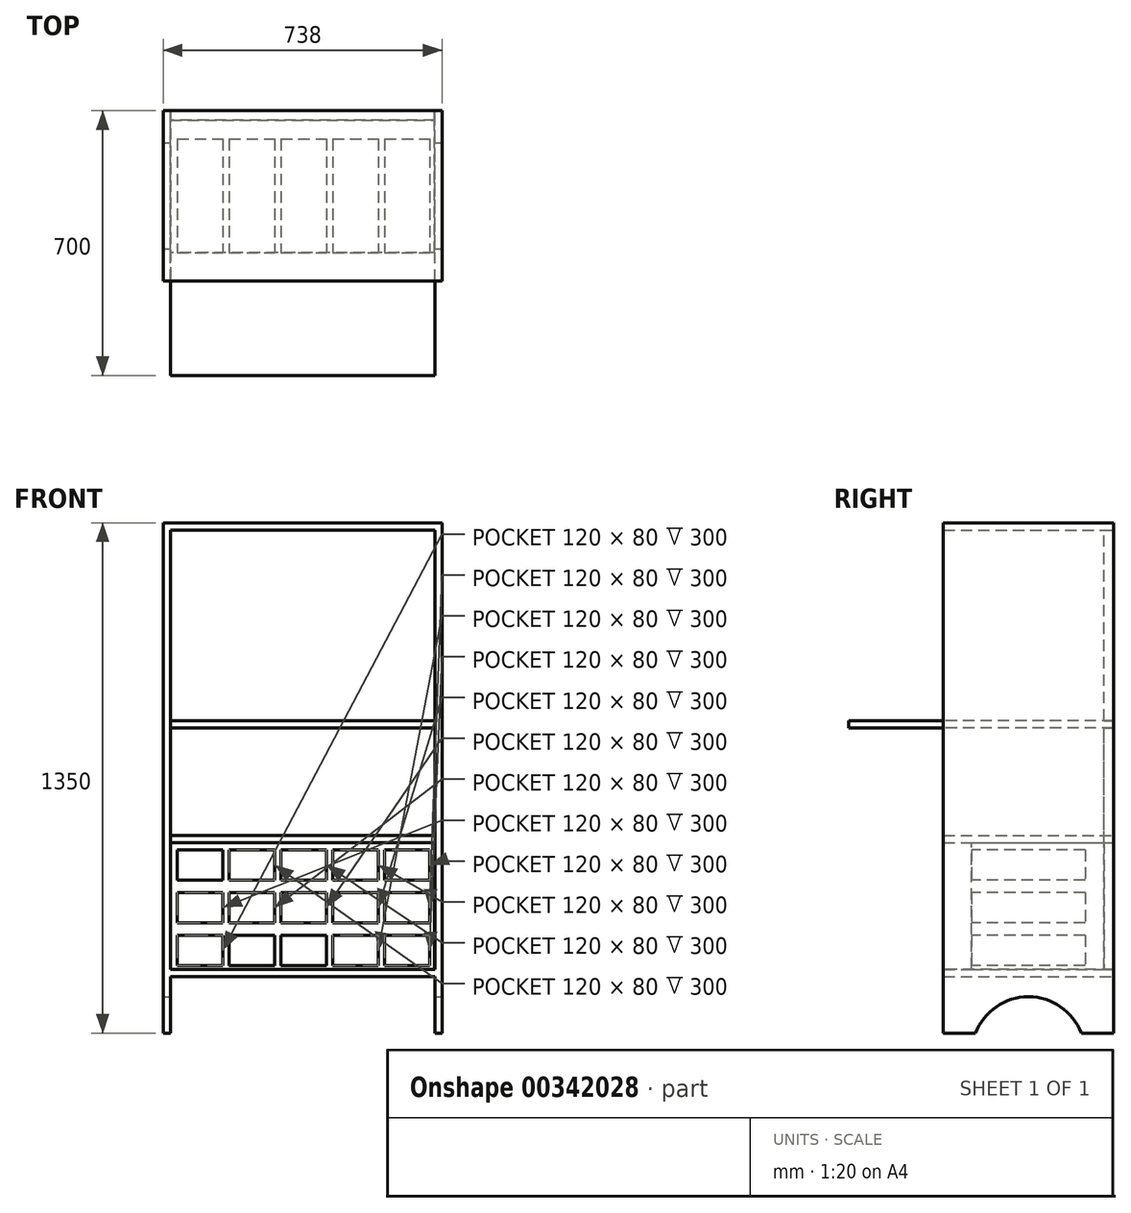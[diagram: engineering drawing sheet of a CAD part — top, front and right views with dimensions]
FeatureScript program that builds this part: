
annotation { "Feature Type Name" : "Feature", "Feature Type Description" : "" }
export const myFeature = defineFeature(function(context is Context, id is Id, definition is map)
    precondition{}
    {
        {
            var Q0;
            Q0=qCreatedBy(makeId("Front.planeOp"),FACE);
            var sketch = newSketch(context, id + "F0", { "sketchPlane" : qUnion([Q0])});
            skLineSegment(sketch, "E0.bottom", {"start": v(-369, 0) * mm, "end": v(-350, 0) * mm});
            skLineSegment(sketch, "E0.top", {"start": v(-369, 1350) * mm, "end": v(-350, 1350) * mm});
            skLineSegment(sketch, "E0.left", {"start": v(-369, 0) * mm, "end": v(-369, 1350) * mm});
            skLineSegment(sketch, "E0.right", {"start": v(-350, 0) * mm, "end": v(-350, 1350) * mm});
            skLineSegment(sketch, "E1", {"start": v(0, 1331) * mm, "end": v(0, 0) * mm, "construction": true});
            skLineSegment(sketch, "E2.MirrorCS", {"start": v(350, 0) * mm, "end": v(350, 1350) * mm});
            skLineSegment(sketch, "E3.MirrorCS", {"start": v(369, 0) * mm, "end": v(350, 0) * mm});
            skLineSegment(sketch, "E4.MirrorCS", {"start": v(369, 0) * mm, "end": v(369, 1350) * mm});
            skLineSegment(sketch, "E5.MirrorCS", {"start": v(369, 1350) * mm, "end": v(350, 1350) * mm});
            skLineSegment(sketch, "E6.bottom", {"start": v(-350, 1350) * mm, "end": v(350, 1350) * mm});
            skLineSegment(sketch, "E6.top", {"start": v(-350, 1331) * mm, "end": v(350, 1331) * mm});
            skLineSegment(sketch, "E6.left", {"start": v(-350, 1350) * mm, "end": v(-350, 1331) * mm});
            skLineSegment(sketch, "E6.right", {"start": v(350, 1350) * mm, "end": v(350, 1331) * mm});
            skSolve(sketch);
        }
        {
            var Q0;
            Q0 = qSketchRegion(id + "F0", true);
            extrude(context, id + "F1", {"entities" : qUnion([Q0]), "depth" : 450 * mm});
        }
        {
            var Q0;
            Q0=makeQuery(id+"F1.opExtrude","SWEPT_FACE",FACE,{"disambiguationData":[OSD([sQuery(id+"F0.wireOp",EDGE,"E0.right")])]});
            var sketch = newSketch(context, id + "F2", { "sketchPlane" : qUnion([Q0])});
            skLineSegment(sketch, "E7.bottom", {"start": v(-450, 826.75) * mm, "end": v(0, 826.75) * mm});
            skLineSegment(sketch, "E7.top", {"start": v(-450, 807.75) * mm, "end": v(0, 807.75) * mm});
            skLineSegment(sketch, "E7.left", {"start": v(-450, 826.75) * mm, "end": v(-450, 807.75) * mm});
            skLineSegment(sketch, "E7.right", {"start": v(0, 826.75) * mm, "end": v(0, 807.75) * mm});
            skLineSegment(sketch, "E8.bottom", {"start": v(-450, 169) * mm, "end": v(0, 169) * mm});
            skLineSegment(sketch, "E8.top", {"start": v(-450, 150) * mm, "end": v(0, 150) * mm});
            skLineSegment(sketch, "E8.left", {"start": v(-450, 169) * mm, "end": v(-450, 150) * mm});
            skLineSegment(sketch, "E8.right", {"start": v(0, 169) * mm, "end": v(0, 150) * mm});
            skSolve(sketch);
        }
        {
            var Q0;
            Q0=makeQuery(id+"F2.imprint","IMPRINT",FACE,{"disambiguationData":[TD([[makeQuery(id+"F2.imprint","IMPRINT",EDGE,{"derivedFrom":sQuery(id+"F2.wireOp",EDGE,"E7.bottom")}),-1.0]])]});
            var Q1;
            Q1=makeQuery(id+"F2.imprint","IMPRINT",FACE,{"disambiguationData":[TD([[makeQuery(id+"F2.imprint","IMPRINT",EDGE,{"derivedFrom":sQuery(id+"F2.wireOp",EDGE,"E8.bottom")}),-1.0]])]});
            var Q2;
            Q2=qCreatedBy(makeId("Right.planeOp"),FACE);
            extrude(context, id + "F3", {"entities" : qUnion([Q0, Q1]), "operationType" : NewBodyOperationType.ADD, "endBound" : BoundingType.UP_TO_NEXT, "endBoundEntityFace" : qUnion([Q2]), "depth" : 25 * mm});
        }
        {
            var Q0;
            Q0=makeQuery(id+"F3.boolean.opBoolean","MERGE",FACE,{"derivedFrom":[makeQuery(id+"F1.opExtrude","CAP_FACE",FACE,{"disambiguationData":[OSD([sQuery(id+"F0.wireOp",EDGE,"E0.bottom"),sQuery(id+"F0.wireOp",EDGE,"E0.top"),sQuery(id+"F0.wireOp",EDGE,"E0.left"),sQuery(id+"F0.wireOp",EDGE,"E0.right"),sQuery(id+"F0.wireOp",EDGE,"KUvRnLVw-DjVN-ga7X-LMZa-ZJt3v3Kkx2uW.bottom"),sQuery(id+"F0.wireOp",EDGE,"KUvRnLVw-DjVN-ga7X-LMZa-ZJt3v3Kkx2uW.top"),sQuery(id+"F0.wireOp",EDGE,"KUvRnLVw-DjVN-ga7X-LMZa-ZJt3v3Kkx2uW.right")])],"isStart":true}),makeQuery(id+"F3.opExtrude","SWEPT_FACE",FACE,{"disambiguationData":[OSD([sQuery(id+"F2.wireOp",EDGE,"E7.right")])]})]});
            var sketch = newSketch(context, id + "F4", { "sketchPlane" : qUnion([Q0])});
            skLineSegment(sketch, "E9.bottom", {"start": v(350, 504.2) * mm, "end": v(-348.68, 504.2) * mm});
            skLineSegment(sketch, "E9.top", {"start": v(350, 154.2) * mm, "end": v(-348.68, 154.2) * mm});
            skLineSegment(sketch, "E9.left", {"start": v(350, 504.2) * mm, "end": v(350, 154.2) * mm});
            skLineSegment(sketch, "E9.right", {"start": v(-348.68, 504.2) * mm, "end": v(-348.68, 154.2) * mm});
            skSolve(sketch);
        }
        {
            var Q0;
            Q0=makeQuery(id+"F4.imprint","IMPRINT",FACE,{"disambiguationData":[TD([[makeQuery(id+"F4.imprint","IMPRINT",EDGE,{"derivedFrom":sQuery(id+"F4.wireOp",EDGE,"E9.bottom")}),1.0]])]});
            extrude(context, id + "F5", {"entities" : qUnion([Q0]), "operationType" : NewBodyOperationType.ADD, "oppositeDirection" : true, "depth" : 375 * mm});
        }
        {
            var Q0;
            Q0=makeQuery(id+"F5.opExtrude","CAP_FACE",FACE,{"disambiguationData":[OSD([sQuery(id+"F4.wireOp",EDGE,"E9.bottom"),sQuery(id+"F4.wireOp",EDGE,"E9.top"),sQuery(id+"F4.wireOp",EDGE,"E9.left"),sQuery(id+"F4.wireOp",EDGE,"E9.right")])],"isStart":false});
            var sketch = newSketch(context, id + "F6", { "sketchPlane" : qUnion([Q0])});
            skLineSegment(sketch, "E10.bottom", {"start": v(-331, 485.2) * mm, "end": v(-211, 485.2) * mm});
            skLineSegment(sketch, "E10.top", {"start": v(-331, 405.2) * mm, "end": v(-211, 405.2) * mm});
            skLineSegment(sketch, "E10.left", {"start": v(-331, 485.2) * mm, "end": v(-331, 405.2) * mm});
            skLineSegment(sketch, "E10.right", {"start": v(-211, 485.2) * mm, "end": v(-211, 405.2) * mm});
            skLineSegment(sketch, "E11.0.1.0", {"start": v(-331, 372) * mm, "end": v(-211, 372) * mm});
            skLineSegment(sketch, "E11.0.1.1", {"start": v(-211, 372) * mm, "end": v(-211, 292) * mm});
            skLineSegment(sketch, "E11.0.1.2", {"start": v(-331, 292) * mm, "end": v(-211, 292) * mm});
            skLineSegment(sketch, "E11.0.1.3", {"start": v(-331, 372) * mm, "end": v(-331, 292) * mm});
            skLineSegment(sketch, "E11.0.2.0", {"start": v(-331, 258.8) * mm, "end": v(-211, 258.8) * mm});
            skLineSegment(sketch, "E11.0.2.1", {"start": v(-211, 258.8) * mm, "end": v(-211, 178.8) * mm});
            skLineSegment(sketch, "E11.0.2.2", {"start": v(-331, 178.8) * mm, "end": v(-211, 178.8) * mm});
            skLineSegment(sketch, "E11.0.2.3", {"start": v(-331, 258.8) * mm, "end": v(-331, 178.8) * mm});
            skLineSegment(sketch, "E11.1.0.0", {"start": v(-194, 485.02) * mm, "end": v(-74, 485.02) * mm});
            skLineSegment(sketch, "E11.1.0.1", {"start": v(-74, 485.02) * mm, "end": v(-74, 405.02) * mm});
            skLineSegment(sketch, "E11.1.0.2", {"start": v(-194, 405.02) * mm, "end": v(-74, 405.02) * mm});
            skLineSegment(sketch, "E11.1.0.3", {"start": v(-194, 485.02) * mm, "end": v(-194, 405.02) * mm});
            skLineSegment(sketch, "E11.1.1.0", {"start": v(-194, 371.82) * mm, "end": v(-74, 371.82) * mm});
            skLineSegment(sketch, "E11.1.1.1", {"start": v(-74, 371.82) * mm, "end": v(-74, 291.82) * mm});
            skLineSegment(sketch, "E11.1.1.2", {"start": v(-194, 291.82) * mm, "end": v(-74, 291.82) * mm});
            skLineSegment(sketch, "E11.1.1.3", {"start": v(-194, 371.82) * mm, "end": v(-194, 291.82) * mm});
            skLineSegment(sketch, "E11.1.2.0", {"start": v(-194, 258.62) * mm, "end": v(-74, 258.62) * mm});
            skLineSegment(sketch, "E11.1.2.1", {"start": v(-74, 258.62) * mm, "end": v(-74, 178.62) * mm});
            skLineSegment(sketch, "E11.1.2.2", {"start": v(-194, 178.62) * mm, "end": v(-74, 178.62) * mm});
            skLineSegment(sketch, "E11.1.2.3", {"start": v(-194, 258.62) * mm, "end": v(-194, 178.62) * mm});
            skLineSegment(sketch, "E11.2.0.0", {"start": v(-57, 484.83) * mm, "end": v(63, 484.83) * mm});
            skLineSegment(sketch, "E11.2.0.1", {"start": v(63, 484.83) * mm, "end": v(63, 404.83) * mm});
            skLineSegment(sketch, "E11.2.0.2", {"start": v(-57, 404.83) * mm, "end": v(63, 404.83) * mm});
            skLineSegment(sketch, "E11.2.0.3", {"start": v(-57, 484.83) * mm, "end": v(-57, 404.83) * mm});
            skLineSegment(sketch, "E11.2.1.0", {"start": v(-57, 371.64) * mm, "end": v(63, 371.64) * mm});
            skLineSegment(sketch, "E11.2.1.1", {"start": v(63, 371.64) * mm, "end": v(63, 291.64) * mm});
            skLineSegment(sketch, "E11.2.1.2", {"start": v(-57, 291.64) * mm, "end": v(63, 291.64) * mm});
            skLineSegment(sketch, "E11.2.1.3", {"start": v(-57, 371.64) * mm, "end": v(-57, 291.64) * mm});
            skLineSegment(sketch, "E11.2.2.0", {"start": v(-57, 258.44) * mm, "end": v(63, 258.44) * mm});
            skLineSegment(sketch, "E11.2.2.1", {"start": v(63, 258.44) * mm, "end": v(63, 178.44) * mm});
            skLineSegment(sketch, "E11.2.2.2", {"start": v(-57, 178.44) * mm, "end": v(63, 178.44) * mm});
            skLineSegment(sketch, "E11.2.2.3", {"start": v(-57, 258.44) * mm, "end": v(-57, 178.44) * mm});
            skLineSegment(sketch, "E11.3.0.0", {"start": v(80, 484.65) * mm, "end": v(200, 484.65) * mm});
            skLineSegment(sketch, "E11.3.0.1", {"start": v(200, 484.65) * mm, "end": v(200, 404.65) * mm});
            skLineSegment(sketch, "E11.3.0.2", {"start": v(80, 404.65) * mm, "end": v(200, 404.65) * mm});
            skLineSegment(sketch, "E11.3.0.3", {"start": v(80, 484.65) * mm, "end": v(80, 404.65) * mm});
            skLineSegment(sketch, "E11.3.1.0", {"start": v(80, 371.45) * mm, "end": v(200, 371.45) * mm});
            skLineSegment(sketch, "E11.3.1.1", {"start": v(200, 371.45) * mm, "end": v(200, 291.45) * mm});
            skLineSegment(sketch, "E11.3.1.2", {"start": v(80, 291.45) * mm, "end": v(200, 291.45) * mm});
            skLineSegment(sketch, "E11.3.1.3", {"start": v(80, 371.45) * mm, "end": v(80, 291.45) * mm});
            skLineSegment(sketch, "E11.3.2.0", {"start": v(80, 258.26) * mm, "end": v(200, 258.26) * mm});
            skLineSegment(sketch, "E11.3.2.1", {"start": v(200, 258.26) * mm, "end": v(200, 178.26) * mm});
            skLineSegment(sketch, "E11.3.2.2", {"start": v(80, 178.26) * mm, "end": v(200, 178.26) * mm});
            skLineSegment(sketch, "E11.3.2.3", {"start": v(80, 258.26) * mm, "end": v(80, 178.26) * mm});
            skLineSegment(sketch, "E11.4.0.0", {"start": v(217, 484.47) * mm, "end": v(337, 484.47) * mm});
            skLineSegment(sketch, "E11.4.0.1", {"start": v(337, 484.47) * mm, "end": v(337, 404.47) * mm});
            skLineSegment(sketch, "E11.4.0.2", {"start": v(217, 404.47) * mm, "end": v(337, 404.47) * mm});
            skLineSegment(sketch, "E11.4.0.3", {"start": v(217, 484.47) * mm, "end": v(217, 404.47) * mm});
            skLineSegment(sketch, "E11.4.1.0", {"start": v(217, 371.27) * mm, "end": v(337, 371.27) * mm});
            skLineSegment(sketch, "E11.4.1.1", {"start": v(337, 371.27) * mm, "end": v(337, 291.27) * mm});
            skLineSegment(sketch, "E11.4.1.2", {"start": v(217, 291.27) * mm, "end": v(337, 291.27) * mm});
            skLineSegment(sketch, "E11.4.1.3", {"start": v(217, 371.27) * mm, "end": v(217, 291.27) * mm});
            skLineSegment(sketch, "E11.4.2.0", {"start": v(217, 258.07) * mm, "end": v(337, 258.07) * mm});
            skLineSegment(sketch, "E11.4.2.1", {"start": v(337, 258.07) * mm, "end": v(337, 178.07) * mm});
            skLineSegment(sketch, "E11.4.2.2", {"start": v(217, 178.07) * mm, "end": v(337, 178.07) * mm});
            skLineSegment(sketch, "E11.4.2.3", {"start": v(217, 258.07) * mm, "end": v(217, 178.07) * mm});
            skLineSegment(sketch, "E11.direction1", {"start": v(-331, 485.2) * mm, "end": v(-194, 485.02) * mm, "construction": true});
            skLineSegment(sketch, "E11.direction2", {"start": v(-331, 485.2) * mm, "end": v(-331, 372) * mm, "construction": true});
            skSolve(sketch);
        }
        {
            var Q0;
            Q0=makeQuery(id+"F6.imprint","IMPRINT",FACE,{"disambiguationData":[TD([[makeQuery(id+"F6.imprint","IMPRINT",EDGE,{"derivedFrom":sQuery(id+"F6.wireOp",EDGE,"E10.bottom")}),-1.0]])]});
            var Q1;
            Q1=makeQuery(id+"F6.imprint","IMPRINT",FACE,{"disambiguationData":[TD([[makeQuery(id+"F6.imprint","IMPRINT",EDGE,{"derivedFrom":sQuery(id+"F6.wireOp",EDGE,"E11.1.0.0")}),-1.0]])]});
            var Q2;
            Q2=makeQuery(id+"F6.imprint","IMPRINT",FACE,{"disambiguationData":[TD([[makeQuery(id+"F6.imprint","IMPRINT",EDGE,{"derivedFrom":sQuery(id+"F6.wireOp",EDGE,"E11.2.0.0")}),-1.0]])]});
            var Q3;
            Q3=makeQuery(id+"F6.imprint","IMPRINT",FACE,{"disambiguationData":[TD([[makeQuery(id+"F6.imprint","IMPRINT",EDGE,{"derivedFrom":sQuery(id+"F6.wireOp",EDGE,"E11.3.0.0")}),-1.0]])]});
            var Q4;
            Q4=makeQuery(id+"F6.imprint","IMPRINT",FACE,{"disambiguationData":[TD([[makeQuery(id+"F6.imprint","IMPRINT",EDGE,{"derivedFrom":sQuery(id+"F6.wireOp",EDGE,"E11.4.0.0")}),-1.0]])]});
            var Q5;
            Q5=makeQuery(id+"F6.imprint","IMPRINT",FACE,{"disambiguationData":[TD([[makeQuery(id+"F6.imprint","IMPRINT",EDGE,{"derivedFrom":sQuery(id+"F6.wireOp",EDGE,"E11.0.1.0")}),-1.0]])]});
            var Q6;
            Q6=makeQuery(id+"F6.imprint","IMPRINT",FACE,{"disambiguationData":[TD([[makeQuery(id+"F6.imprint","IMPRINT",EDGE,{"derivedFrom":sQuery(id+"F6.wireOp",EDGE,"E11.1.1.0")}),-1.0]])]});
            var Q7;
            Q7=makeQuery(id+"F6.imprint","IMPRINT",FACE,{"disambiguationData":[TD([[makeQuery(id+"F6.imprint","IMPRINT",EDGE,{"derivedFrom":sQuery(id+"F6.wireOp",EDGE,"E11.2.1.0")}),-1.0]])]});
            var Q8;
            Q8=makeQuery(id+"F6.imprint","IMPRINT",FACE,{"disambiguationData":[TD([[makeQuery(id+"F6.imprint","IMPRINT",EDGE,{"derivedFrom":sQuery(id+"F6.wireOp",EDGE,"E11.3.1.0")}),-1.0]])]});
            var Q9;
            Q9=makeQuery(id+"F6.imprint","IMPRINT",FACE,{"disambiguationData":[TD([[makeQuery(id+"F6.imprint","IMPRINT",EDGE,{"derivedFrom":sQuery(id+"F6.wireOp",EDGE,"E11.4.1.0")}),-1.0]])]});
            var Q10;
            Q10=makeQuery(id+"F6.imprint","IMPRINT",FACE,{"disambiguationData":[TD([[makeQuery(id+"F6.imprint","IMPRINT",EDGE,{"derivedFrom":sQuery(id+"F6.wireOp",EDGE,"E11.0.2.0")}),-1.0]])]});
            var Q11;
            Q11=makeQuery(id+"F6.imprint","IMPRINT",FACE,{"disambiguationData":[TD([[makeQuery(id+"F6.imprint","IMPRINT",EDGE,{"derivedFrom":sQuery(id+"F6.wireOp",EDGE,"E11.1.2.0")}),-1.0]])]});
            var Q12;
            Q12=makeQuery(id+"F6.imprint","IMPRINT",FACE,{"disambiguationData":[TD([[makeQuery(id+"F6.imprint","IMPRINT",EDGE,{"derivedFrom":sQuery(id+"F6.wireOp",EDGE,"E11.2.2.0")}),-1.0]])]});
            var Q13;
            Q13=makeQuery(id+"F6.imprint","IMPRINT",FACE,{"disambiguationData":[TD([[makeQuery(id+"F6.imprint","IMPRINT",EDGE,{"derivedFrom":sQuery(id+"F6.wireOp",EDGE,"E11.3.2.0")}),-1.0]])]});
            var Q14;
            Q14=makeQuery(id+"F6.imprint","IMPRINT",FACE,{"disambiguationData":[TD([[makeQuery(id+"F6.imprint","IMPRINT",EDGE,{"derivedFrom":sQuery(id+"F6.wireOp",EDGE,"E11.4.2.0")}),-1.0]])]});
            extrude(context, id + "F7", {"entities" : qUnion([Q0, Q1, Q2, Q3, Q4, Q5, Q6, Q7, Q8, Q9, Q10, Q11, Q12, Q13, Q14]), "operationType" : NewBodyOperationType.REMOVE, "oppositeDirection" : true, "depth" : 300 * mm});
        }
        {
            var Q0;
            Q0=makeQuery(id+"F1.opExtrude","SWEPT_FACE",FACE,{"disambiguationData":[OSD([sQuery(id+"F0.wireOp",EDGE,"E4.MirrorCS")])]});
            var sketch = newSketch(context, id + "F8", { "sketchPlane" : qUnion([Q0])});
            skArc(sketch, "E12", {"start": v(-85, 0) * mm, "mid": v(-225, 96.15) * mm, "end": v(-365, 0) * mm});
            skLineSegment(sketch, "E13", {"start": v(-365, 0) * mm, "end": v(-85, 0) * mm});
            skSolve(sketch);
        }
        {
            var Q0;
            Q0 = qSketchRegion(id + "F8", true);
            extrude(context, id + "F9", {"entities" : qUnion([Q0]), "operationType" : NewBodyOperationType.REMOVE, "endBound" : BoundingType.THROUGH_ALL, "oppositeDirection" : true, "depth" : 25 * mm});
        }
        {
            var Q0;
            {var subQ0=sQuery(id+"F2.wireOp",EDGE,"E8.right");var subQ1=sQuery(id+"F0.wireOp",EDGE,"E0.right");Q0=makeQuery(id+"F5.boolean.opBoolean","MERGE",FACE,{"derivedFrom":[makeQuery(id+"F3.boolean.opBoolean","MERGE",FACE,{"derivedFrom":[makeQuery(id+"F1.opExtrude","CAP_FACE",FACE,{"disambiguationData":[OSD([sQuery(id+"F0.wireOp",EDGE,"E0.bottom"),sQuery(id+"F0.wireOp",EDGE,"E0.top"),sQuery(id+"F0.wireOp",EDGE,"E0.left"),subQ1,sQuery(id+"F0.wireOp",EDGE,"E2.MirrorCS"),sQuery(id+"F0.wireOp",EDGE,"E3.MirrorCS"),sQuery(id+"F0.wireOp",EDGE,"E4.MirrorCS"),sQuery(id+"F0.wireOp",EDGE,"E5.MirrorCS"),sQuery(id+"F0.wireOp",EDGE,"E6.bottom"),sQuery(id+"F0.wireOp",EDGE,"E6.top")])],"isStart":true}),makeQuery(id+"F3.opExtrude","SWEPT_FACE",FACE,{"disambiguationData":[OSD([sQuery(id+"F2.wireOp",EDGE,"E7.right")])]}),makeQuery(id+"F3.opExtrude","SWEPT_FACE",FACE,{"disambiguationData":[OSD([subQ0])]})]}),makeQuery(id+"F5.opExtrude","CAP_FACE",FACE,{"disambiguationData":[OSD([subQ1,sQuery(id+"F2.wireOp",EDGE,"E8.bottom"),subQ0,sQuery(id+"F4.wireOp",EDGE,"E9.bottom"),sQuery(id+"F4.wireOp",EDGE,"E9.left"),sQuery(id+"F4.wireOp",EDGE,"E9.right")])],"isStart":true})]});}
            var sketch = newSketch(context, id + "F10", { "sketchPlane" : qUnion([Q0])});
            skLineSegment(sketch, "E14.bottom", {"start": v(-350, 1331) * mm, "end": v(350, 1331) * mm});
            skLineSegment(sketch, "E14.top", {"start": v(-350, 826.75) * mm, "end": v(350, 826.75) * mm});
            skLineSegment(sketch, "E14.left", {"start": v(-350, 1331) * mm, "end": v(-350, 826.75) * mm});
            skLineSegment(sketch, "E14.right", {"start": v(350, 1331) * mm, "end": v(350, 826.75) * mm});
            skSolve(sketch);
        }
        {
            var Q0;
            Q0=makeQuery(id+"F10.imprint","IMPRINT",FACE,{"disambiguationData":[TD([[makeQuery(id+"F10.imprint","IMPRINT",EDGE,{"derivedFrom":sQuery(id+"F10.wireOp",EDGE,"E14.bottom")}),1.0]])]});
            extrude(context, id + "F11", {"entities" : qUnion([Q0]), "oppositeDirection" : true, "depth" : 25 * mm});
        }
        {
            var Q0;
            {var subQ0=sQuery(id+"F2.wireOp",EDGE,"E8.right");var subQ1=sQuery(id+"F0.wireOp",EDGE,"E0.right");Q0=makeQuery(id+"F5.boolean.opBoolean","MERGE",FACE,{"derivedFrom":[makeQuery(id+"F3.boolean.opBoolean","MERGE",FACE,{"derivedFrom":[makeQuery(id+"F1.opExtrude","CAP_FACE",FACE,{"disambiguationData":[OSD([sQuery(id+"F0.wireOp",EDGE,"E0.bottom"),sQuery(id+"F0.wireOp",EDGE,"E0.top"),sQuery(id+"F0.wireOp",EDGE,"E0.left"),subQ1,sQuery(id+"F0.wireOp",EDGE,"E2.MirrorCS"),sQuery(id+"F0.wireOp",EDGE,"E3.MirrorCS"),sQuery(id+"F0.wireOp",EDGE,"E4.MirrorCS"),sQuery(id+"F0.wireOp",EDGE,"E5.MirrorCS"),sQuery(id+"F0.wireOp",EDGE,"E6.bottom"),sQuery(id+"F0.wireOp",EDGE,"E6.top")])],"isStart":true}),makeQuery(id+"F3.opExtrude","SWEPT_FACE",FACE,{"disambiguationData":[OSD([sQuery(id+"F2.wireOp",EDGE,"E7.right")])]}),makeQuery(id+"F3.opExtrude","SWEPT_FACE",FACE,{"disambiguationData":[OSD([subQ0])]})]}),makeQuery(id+"F5.opExtrude","CAP_FACE",FACE,{"disambiguationData":[OSD([subQ1,sQuery(id+"F2.wireOp",EDGE,"E8.bottom"),subQ0,sQuery(id+"F4.wireOp",EDGE,"E9.bottom"),sQuery(id+"F4.wireOp",EDGE,"E9.left"),sQuery(id+"F4.wireOp",EDGE,"E9.right")])],"isStart":true})]});}
            var sketch = newSketch(context, id + "F12", { "sketchPlane" : qUnion([Q0])});
            skSolve(sketch);
        }
        {
            var Q0;
            Q0=makeQuery(id+"F12.imprint","IMPRINT",FACE,{"disambiguationData":[TD([[makeQuery(id+"F12.imprint","IMPRINT",EDGE,{"derivedFrom":makeQuery(id+"F5.opExtrude","CAP_EDGE",EDGE,{"disambiguationData":[OSD([sQuery(id+"F4.wireOp",EDGE,"E9.bottom")])],"isStart":true})}),-1.0]])]});
            extrude(context, id + "F13", {"entities" : qUnion([Q0]), "oppositeDirection" : true, "depth" : 25 * mm});
        }
        {
            var Q0;
            {var subQ6=sQuery(id+"F0.wireOp",EDGE,"E0.right");Q0=makeQuery(id+"F3.boolean.opBoolean","SPLIT",FACE,{"disambiguationData":[TD([makeQuery(id+"F3.opExtrude","SWEPT_FACE",FACE,{"disambiguationData":[OSD([sQuery(id+"F2.wireOp",EDGE,"E7.top")])]})])],"derivedFrom":makeQuery(id+"F1.opExtrude","SWEPT_FACE",FACE,{"disambiguationData":[OSD([subQ6])]})});}
            var sketch = newSketch(context, id + "F14", { "sketchPlane" : qUnion([Q0])});
            skLineSegment(sketch, "E15.bottom", {"start": v(0, 523.2) * mm, "end": v(-450, 523.2) * mm});
            skLineSegment(sketch, "E15.top", {"start": v(0, 504.2) * mm, "end": v(-450, 504.2) * mm});
            skLineSegment(sketch, "E15.left", {"start": v(0, 523.2) * mm, "end": v(0, 504.2) * mm});
            skLineSegment(sketch, "E15.right", {"start": v(-450, 523.2) * mm, "end": v(-450, 504.2) * mm});
            skSolve(sketch);
        }
        {
            var Q0;
            Q0=makeQuery(id+"F14.imprint","IMPRINT",FACE,{"disambiguationData":[TD([[makeQuery(id+"F14.imprint","IMPRINT",EDGE,{"derivedFrom":sQuery(id+"F14.wireOp",EDGE,"E15.bottom")}),1.0]])]});
            extrude(context, id + "F15", {"entities" : qUnion([Q0]), "endBound" : BoundingType.UP_TO_NEXT, "depth" : 25 * mm});
        }
        {
            var Q0;
            Q0=makeQuery(id+"F3.boolean.opBoolean","MERGE",FACE,{"derivedFrom":[makeQuery(id+"F1.opExtrude","CAP_FACE",FACE,{"disambiguationData":[OSD([sQuery(id+"F0.wireOp",EDGE,"E0.bottom"),sQuery(id+"F0.wireOp",EDGE,"E0.top"),sQuery(id+"F0.wireOp",EDGE,"E0.left"),sQuery(id+"F0.wireOp",EDGE,"E0.right"),sQuery(id+"F0.wireOp",EDGE,"E2.MirrorCS"),sQuery(id+"F0.wireOp",EDGE,"E3.MirrorCS"),sQuery(id+"F0.wireOp",EDGE,"E4.MirrorCS"),sQuery(id+"F0.wireOp",EDGE,"E5.MirrorCS"),sQuery(id+"F0.wireOp",EDGE,"E6.bottom"),sQuery(id+"F0.wireOp",EDGE,"E6.top")])],"isStart":false}),makeQuery(id+"F3.opExtrude","SWEPT_FACE",FACE,{"disambiguationData":[OSD([sQuery(id+"F2.wireOp",EDGE,"E7.left")])]}),makeQuery(id+"F3.opExtrude","SWEPT_FACE",FACE,{"disambiguationData":[OSD([sQuery(id+"F2.wireOp",EDGE,"E8.left")])]})]});
            var sketch = newSketch(context, id + "F16", { "sketchPlane" : qUnion([Q0])});
            skLineSegment(sketch, "E16.bottom", {"start": v(-350, 826.75) * mm, "end": v(350, 826.75) * mm});
            skLineSegment(sketch, "E16.top", {"start": v(-350, 807.75) * mm, "end": v(350, 807.75) * mm});
            skLineSegment(sketch, "E16.left", {"start": v(-350, 826.75) * mm, "end": v(-350, 807.75) * mm});
            skLineSegment(sketch, "E16.right", {"start": v(350, 826.75) * mm, "end": v(350, 807.75) * mm});
            skSolve(sketch);
        }
        {
            var Q0;
            Q0=makeQuery(id+"F16.imprint","IMPRINT",FACE,{"disambiguationData":[TD([[makeQuery(id+"F16.imprint","IMPRINT",EDGE,{"derivedFrom":sQuery(id+"F16.wireOp",EDGE,"E16.bottom")}),1.0]])]});
            extrude(context, id + "F17", {"entities" : qUnion([Q0]), "operationType" : NewBodyOperationType.ADD, "depth" : 250 * mm});
        }
    });
